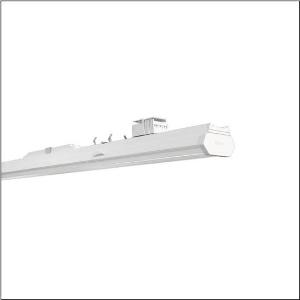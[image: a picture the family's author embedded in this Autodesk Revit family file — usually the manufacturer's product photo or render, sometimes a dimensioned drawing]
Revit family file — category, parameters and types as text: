
# Revit family: licross_r__21_protected_mo_52td1bvn48xg_aeae
name_source: partatom
category: Lighting Fixtures
units: mm (PartAtom-declared; Revit-internal decimal feet)

## family parameters
Cut with Voids When Loaded = No
Host = Face
Light Source = No
Part Type = Normal
Room Calculation Point = No
Round Connector Dimension = Use Diameter
Shared = No

## types (1)
- --- (1 x LED, 8000 lm, 48.3 W, 4000K)
    Apparent Load = 48 VA
    CIE Flux Codes = 54 82 95 97 100
    Color Rendering = 80
    Color Temperature = 4000K
    Default Elevation = 1800 mm
    Description = Licross® 21 Protected MO, luminaire insert, of sheet steel, galvanised, coil coated, white, length: 1.500mm, width: 90mm, height: 101mm, LED rated luminous flux: 8.000lm, light colour: 840, control gear: DALI 2, CLO, with plug, 5-pole, with phase selection, mains connection: 220..240V, AC, 50/60Hz, start of lifetime: 48W, end of service life: 58W, halogen-free wiring, primary optical cover: cover, of PMMA, light emission: direct distribution, primary light characteristic: symmetric, protection rating (complete): IP54, insulation class (complete): insulation class I (protective earthing), certification: CE, ENEC, VDE, UKCA, protection symbol: D if used in an environment with non-conductive dust loads with corresponding accessories, impact resistance: IK06, permissible ambient temperature for indoor applications: -25..+40°C, corresponds to IFS (International Featured Standards) requirements for safety and quality in the food industry, reducing of maximum allowable ambient temperature of 5°C with ceiling mounting, LABS conformity tested according to VDMA 24364:2018-05, packaging unit: 1 piece
    Height = 92 mm
    Lamp = 1 x LED
    Lamp Light Flux = 8000 lm
    Lamp Power = 48.3 W
    Lamp count = 1
    Length = 1500 mm
    Luminous efficacy = 166 lm/W
    Manufacturer = Siteco
    ModVariant = No
    Model = 52TD1BVN48XG
    Mounting Place = Ceiling
    Mounting Type = Pendant
    Number of Poles = 1
    OnlyDefault = Yes
    Power Factor = 1
    Product Name = Licross® 21 Protected MO
    Product group = luminaire insert
    ProductGroupID = 901
    Protection Class = Protection class I
    Protection Degree = IP 54
    RLX_Detail_Level = 1
    RLX_Emergency_Light_Flux = 0 lm
    RLX_Emergency_Type = 0
    RLX_Emergency_Type_DB = No
    RlxData = <blob elided: 24269 chars, md5=b264ef48>
    Socket = socket
    Standby Power = 0 W
    System Light Flux = 8000 lm
    System Power = 48 W
    Type Comments = factory setting: luminous flux: 100 % | dim-lin: 254 | 326 mA
    Type Image = l_1256148.jpg
    URL = http://relux.com
    VarID = @adj_052185
    Voltage = 0 V
    Weight = 0.00 kg
    Width = 88 mm

## geometry (parser evidence)
native form markers: Blend x4, Sweep x11
no freeform markers — native parametric forms only
